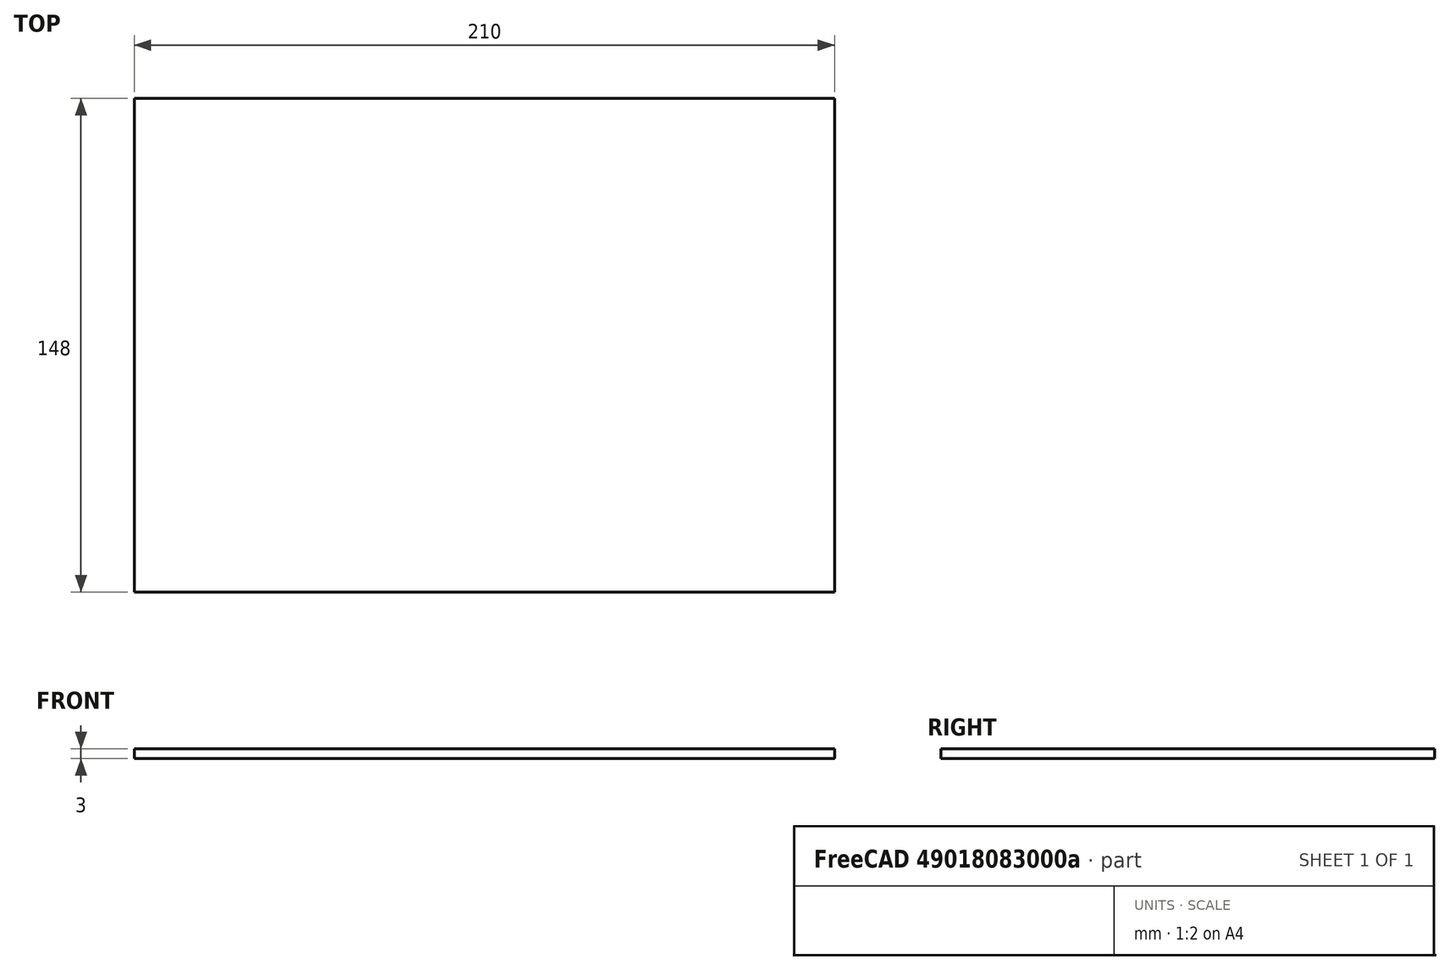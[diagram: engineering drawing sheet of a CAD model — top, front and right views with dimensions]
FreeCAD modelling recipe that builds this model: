
FCSTD DOCUMENT  (FreeCAD 0.20R29177 (Git))
Label: 1001_keyboard_button_labels_A5
License: All rights reserved
LicenseURL: http://en.wikipedia.org/wiki/All_rights_reserved
objects: Sketcher::SketchObject×5, PartDesign::Pad×1, PartDesign::Body×1
note: 8 computed .brp shape members not serialized (recipe doc carries the construction recipe); baked Part::Feature solids carry a one-line shape summary decoded from their .brp

FEATURE [Sketcher::SketchObject] Sketch
  FullyConstrained = true
  MapMode = 5
  Support = -> [XY_Plane]
  sketch-geometry (5):
    g0: LineSegment StartX=0 StartY=148 StartZ=0 EndX=210 EndY=148 EndZ=0
    g1: LineSegment StartX=210 StartY=148 StartZ=0 EndX=210 EndY=0 EndZ=0
    g2: LineSegment StartX=210 StartY=0 StartZ=0 EndX=0 EndY=0 EndZ=0
    g3: LineSegment StartX=0 StartY=0 StartZ=0 EndX=0 EndY=74 EndZ=0
    g4: LineSegment StartX=0 StartY=74 StartZ=0 EndX=0 EndY=148 EndZ=0
  constraints (14):
    c: Coincident(g0,g1)
    c: Coincident(g1,g2)
    c: Horizontal(g0)
    c: Horizontal(g2)
    c: Vertical(g1)
    c: DistanceY(g1,g1) = 148
    c: DistanceX(g0,g0) = 210
    c: Coincident(g3,g2)
    c: Coincident(g4,g0)
    c: Equal(g3,g4)
    c: Vertical(g4)
    c: Vertical(g3)
    c: Coincident(g3,g4)
    c: Coincident(g2,g-1)
FEATURE [PartDesign::Pad] Pad  label="A4_Landscape"
  AllowMultiFace = false
  Direction = (0,0,1)
  Length = 3
  Length2 = 100
  Profile = -> Sketch
  ReferenceAxis = -> Sketch [N_Axis]
  Type = 0
FEATURE [Sketcher::SketchObject] Sketch002  label="ButtonsLayoutSquare"
  FullyConstrained = false
  sketch-geometry (15):
    g0: LineSegment StartX=28.3334 StartY=64.9582 StartZ=0 EndX=28.3334 EndY=24.9582 EndZ=0
    g1: Circle CenterX=28.3334 CenterY=64.9582 CenterZ=0 NormalX=0 NormalY=0 NormalZ=1 AngleXU=0 Radius=15
    g2: Circle CenterX=28.3334 CenterY=24.9582 CenterZ=0 NormalX=0 NormalY=0 NormalZ=1 AngleXU=0 Radius=15
    g3: LineSegment StartX=28.3334 StartY=64.9582 StartZ=0 EndX=68.3334 EndY=64.9582 EndZ=0
    g4: LineSegment StartX=28.3334 StartY=24.9582 StartZ=0 EndX=68.3334 EndY=24.9582 EndZ=0
    g5: LineSegment StartX=68.3334 StartY=24.9582 StartZ=0 EndX=68.3334 EndY=64.9582 EndZ=0
    g6: Circle CenterX=68.3334 CenterY=64.9582 CenterZ=0 NormalX=0 NormalY=0 NormalZ=1 AngleXU=0 Radius=14.5
    g7: Circle CenterX=68.3334 CenterY=24.9582 CenterZ=0 NormalX=0 NormalY=0 NormalZ=1 AngleXU=0 Radius=15
    g8: LineSegment StartX=28.3334 StartY=24.9582 StartZ=0 EndX=48.3334 EndY=44.9582 EndZ=0
    g9: LineSegment StartX=48.3334 StartY=44.9582 StartZ=0 EndX=68.3334 EndY=64.9582 EndZ=0
    g10: LineSegment StartX=8.33338 StartY=84.9582 StartZ=0 EndX=8.33338 EndY=4.95818 EndZ=0
    g11: LineSegment StartX=8.33338 StartY=4.95818 StartZ=0 EndX=88.3334 EndY=4.95818 EndZ=0
    g12: LineSegment StartX=88.3334 StartY=4.95818 StartZ=0 EndX=88.3334 EndY=84.9582 EndZ=0
    g13: LineSegment StartX=88.3334 StartY=84.9582 StartZ=0 EndX=8.33338 EndY=84.9582 EndZ=0
    g14: Circle CenterX=48.3334 CenterY=44.9582 CenterZ=0 NormalX=0 NormalY=0 NormalZ=1 AngleXU=0 Radius=56.5685
  constraints (35):
    c: Equal(g2,g1)
    c: Coincident(g3,g1)
    c: Coincident(g4,g2)
    c: Coincident(g5,g4)
    c: Coincident(g5,g3)
    c: Equal(g3,g5)
    c: Equal(g5,g4)
    c: Coincident(g6,g3)
    c: Coincident(g7,g4)
    c: Coincident(g1,g0)
    c: Coincident(g0,g2)
    c: Angle(g0,g3) = 1.5708
    c: Distance(g6,g1) = 40
    c: Diameter(g6) = 29
    c: Vertical(g5)
    c: Vertical(g0)
    c: Coincident(g8,g2)
    c: Coincident(g9,g8)
    c: Coincident(g9,g6)
    c: Equal(g9,g8)
    c: Parallel(g9,g8)
    c: Coincident(g10,g11)
    c: Coincident(g11,g12)
    c: Coincident(g12,g13)
    c: Coincident(g13,g10)
    c: Equal(g10,g11)
    c: Equal(g10,g12)
    c: Equal(g10,g13)
    c: PointOnObject(g10,g14)
    c: PointOnObject(g11,g14)
    c: PointOnObject(g12,g14)
    c: PointOnObject(g13,g14)
    c: Coincident(g14,g8)
    c: Horizontal(g13)
    c: DistanceX(g13,g13) = 80
FEATURE [Sketcher::SketchObject] Sketch008  label="ButtonsLayoutLTLS"
  FullyConstrained = false
  sketch-geometry (20):
    g0: Circle CenterX=128.028 CenterY=71.1546 CenterZ=0 NormalX=0 NormalY=0 NormalZ=1 AngleXU=0 Radius=15
    g1: Circle CenterX=168.028 CenterY=71.1546 CenterZ=0 NormalX=0 NormalY=0 NormalZ=1 AngleXU=0 Radius=14.5
    g2: LineSegment StartX=188.028 StartY=91.1546 StartZ=0 EndX=108.028 EndY=91.1546 EndZ=0
    g3: LineSegment StartX=148.028 StartY=51.1546 StartZ=0 EndX=108.028 EndY=51.1546 EndZ=0
    g4: LineSegment StartX=148.028 StartY=51.1546 StartZ=0 EndX=188.028 EndY=51.1546 EndZ=0
    g5: LineSegment StartX=188.028 StartY=91.1546 StartZ=0 EndX=188.028 EndY=51.1546 EndZ=0
    g6: LineSegment StartX=108.028 StartY=91.1546 StartZ=0 EndX=108.028 EndY=71.1546 EndZ=0
    g7: LineSegment StartX=108.028 StartY=71.1546 StartZ=0 EndX=108.028 EndY=51.1546 EndZ=0
    g8: LineSegment StartX=128.028 StartY=71.1546 StartZ=0 EndX=148.028 EndY=71.1546 EndZ=0
    g9: LineSegment StartX=148.028 StartY=71.1546 StartZ=0 EndX=168.028 EndY=71.1546 EndZ=0
    g10: Circle CenterX=128.715 CenterY=25.6447 CenterZ=0 NormalX=0 NormalY=0 NormalZ=1 AngleXU=0 Radius=15
    g11: Circle CenterX=168.715 CenterY=25.6447 CenterZ=0 NormalX=0 NormalY=0 NormalZ=1 AngleXU=0 Radius=14.5
    g12: LineSegment StartX=188.715 StartY=45.6447 StartZ=0 EndX=108.715 EndY=45.6447 EndZ=0
    g13: LineSegment StartX=148.715 StartY=5.64469 StartZ=0 EndX=108.715 EndY=5.64469 EndZ=0
    g14: LineSegment StartX=148.715 StartY=5.64469 StartZ=0 EndX=188.715 EndY=5.64469 EndZ=0
    g15: LineSegment StartX=188.715 StartY=45.6447 StartZ=0 EndX=188.715 EndY=5.64469 EndZ=0
    g16: LineSegment StartX=108.715 StartY=45.6447 StartZ=0 EndX=108.715 EndY=25.6447 EndZ=0
    g17: LineSegment StartX=108.715 StartY=25.6447 StartZ=0 EndX=108.715 EndY=5.64469 EndZ=0
    g18: LineSegment StartX=128.715 StartY=25.6447 StartZ=0 EndX=148.715 EndY=25.6447 EndZ=0
    g19: LineSegment StartX=148.715 StartY=25.6447 StartZ=0 EndX=168.715 EndY=25.6447 EndZ=0
  constraints (52):
    c: Distance(g1,g0) = 40
    c: Diameter(g1) = 29
    c: Horizontal(g2)
    c: DistanceX(g2,g2) = 80
    c: Horizontal(g3)
    c: Coincident(g4,g3)
    c: Horizontal(g4)
    c: Coincident(g5,g2)
    c: Coincident(g5,g4)
    c: Vertical(g5)
    c: Coincident(g6,g2)
    c: Vertical(g6)
    c: Coincident(g7,g6)
    c: Coincident(g7,g3)
    c: Vertical(g7)
    c: Coincident(g8,g0)
    c: Horizontal(g8)
    c: Coincident(g9,g8)
    c: Coincident(g9,g1)
    c: Horizontal(g9)
    c: Horizontal(g0,g6)
    c: Vertical(g8,g3)
    c: Equal(g7,g6)
    c: Equal(g4,g3)
    c: Equal(g9,g8)
    c: DistanceY(g5,g5) = 40
    c: Distance(g11,g10) = 40
    c: Diameter(g11) = 29
    c: Horizontal(g12)
    c: DistanceX(g12,g12) = 80
    c: Horizontal(g13)
    c: Coincident(g14,g13)
    c: Horizontal(g14)
    c: Coincident(g15,g12)
    c: Coincident(g15,g14)
    c: Vertical(g15)
    c: Coincident(g16,g12)
    c: Vertical(g16)
    c: Coincident(g17,g16)
    c: Coincident(g17,g13)
    c: Vertical(g17)
    c: Coincident(g18,g10)
    c: Horizontal(g18)
    c: Coincident(g19,g18)
    c: Coincident(g19,g11)
    c: Horizontal(g19)
    c: Horizontal(g10,g16)
    c: Vertical(g18,g13)
    c: Equal(g17,g16)
    c: Equal(g14,g13)
    c: Equal(g19,g18)
    c: DistanceY(g15,g15) = 40
FEATURE [Sketcher::SketchObject] Sketch009  label="ButtonsLayoutSelHotStart"
  FullyConstrained = false
  sketch-geometry (12):
    g0: Circle CenterX=68.3334 CenterY=117.764 CenterZ=0 NormalX=0 NormalY=0 NormalZ=1 AngleXU=0 Radius=15
    g1: Circle CenterX=28.3334 CenterY=117.764 CenterZ=0 NormalX=0 NormalY=0 NormalZ=1 AngleXU=0 Radius=15
    g2: LineSegment StartX=68.3334 StartY=117.764 StartZ=0 EndX=108.333 EndY=117.764 EndZ=0
    g3: Circle CenterX=108.333 CenterY=117.764 CenterZ=0 NormalX=0 NormalY=0 NormalZ=1 AngleXU=0 Radius=14.5
    g4: LineSegment StartX=68.3334 StartY=117.764 StartZ=0 EndX=28.3334 EndY=117.764 EndZ=0
    g5: LineSegment StartX=68.3334 StartY=117.764 StartZ=0 EndX=68.3334 EndY=137.764 EndZ=0
    g6: LineSegment StartX=68.3334 StartY=137.764 StartZ=0 EndX=8.33338 EndY=137.764 EndZ=0
    g7: LineSegment StartX=8.33338 StartY=137.764 StartZ=0 EndX=8.33338 EndY=97.764 EndZ=0
    g8: LineSegment StartX=8.33338 StartY=97.764 StartZ=0 EndX=128.333 EndY=97.764 EndZ=0
    g9: LineSegment StartX=128.333 StartY=97.764 StartZ=0 EndX=128.333 EndY=117.764 EndZ=0
    g10: LineSegment StartX=128.333 StartY=117.764 StartZ=0 EndX=128.333 EndY=137.764 EndZ=0
    g11: LineSegment StartX=128.333 StartY=137.764 StartZ=0 EndX=68.3334 EndY=137.764 EndZ=0
  constraints (30):
    c: Equal(g1,g0)
    c: Coincident(g2,g0)
    c: Coincident(g3,g2)
    c: Distance(g3,g0) = 40
    c: Diameter(g3) = 29
    c: Coincident(g4,g0)
    c: Coincident(g4,g1)
    c: Equal(g4,g2)
    c: Horizontal(g4)
    c: Coincident(g5,g0)
    c: Vertical(g5)
    c: Coincident(g6,g5)
    c: Horizontal(g6)
    c: Coincident(g7,g6)
    c: Vertical(g7)
    c: Horizontal(g8)
    c: Coincident(g9,g8)
    c: Vertical(g9)
    c: Coincident(g10,g9)
    c: Vertical(g10)
    c: Coincident(g11,g10)
    c: Coincident(g11,g6)
    c: Horizontal(g11)
    c: Horizontal(g9,g3)
    c: Equal(g11,g6)
    c: Coincident(g8,g7)
    c: Equal(g9,g10)
    c: Horizontal(g2)
    c: DistanceY(g7,g7) = 40
    c: DistanceX(g6,g10) = 120
FEATURE [Sketcher::SketchObject] Sketch010
  FullyConstrained = false
  MapMode = 5
  Support = -> [XY_Plane]
  sketch-geometry (45):
    g0: Circle CenterX=68.0905 CenterY=65.8823 CenterZ=0 NormalX=0 NormalY=0 NormalZ=1 AngleXU=0 Radius=9
    g1: LineSegment StartX=65.5172 StartY=59.9412 StartZ=0 EndX=62.9322 EndY=59.9412 EndZ=0
    g2: LineSegment StartX=62.9322 StartY=59.9412 StartZ=0 EndX=66.087 EndY=71.9412 EndZ=0
    g3: LineSegment StartX=66.087 StartY=71.9412 StartZ=0 EndX=67.512 EndY=67.529 EndZ=0
    g4: LineSegment StartX=67.512 StartY=67.529 StartZ=0 EndX=65.5172 EndY=59.9412 EndZ=0
    g5: LineSegment StartX=67.1378 StartY=71.9412 StartZ=0 EndX=69.765 EndY=71.9412 EndZ=0
    g6: LineSegment StartX=69.765 StartY=71.9412 StartZ=0 EndX=73.6407 EndY=59.9412 EndZ=0
    g7: LineSegment StartX=73.6407 StartY=59.9412 StartZ=0 EndX=71.0558 EndY=59.9412 EndZ=0
    g8: LineSegment StartX=71.0558 StartY=59.9412 StartZ=0 EndX=70.2347 EndY=62.4835 EndZ=0
    g9: LineSegment StartX=68.0835 StartY=64.9835 StartZ=0 EndX=69.385 EndY=64.9835 EndZ=0
    g10: LineSegment StartX=69.385 StartY=64.9835 StartZ=0 EndX=67.1378 EndY=71.9412 EndZ=0
    g11: LineSegment StartX=67.512 StartY=67.529 StartZ=0 EndX=65.0941 EndY=68.1646 EndZ=0
    g12: LineSegment StartX=70.2347 StartY=62.4835 StartZ=0 EndX=67.4263 EndY=62.4835 EndZ=0
    g13: LineSegment StartX=67.4263 StartY=62.4835 StartZ=0 EndX=68.0835 EndY=64.9835 EndZ=0
    g14: LineSegment StartX=69.385 StartY=64.9835 StartZ=0 EndX=71.764 EndY=65.7518 EndZ=0
    g15: LineSegment StartX=69.385 StartY=64.9835 StartZ=0 EndX=69.385 EndY=62.4835 EndZ=0
    g16: Circle CenterX=28.3099 CenterY=64.6257 CenterZ=0 NormalX=0 NormalY=0 NormalZ=1 AngleXU=0 Radius=9
    g17: LineSegment StartX=24.5219 StartY=70.219 StartZ=0 EndX=24.5219 EndY=59.0563 EndZ=0
    g18: LineSegment StartX=24.5219 StartY=59.0563 StartZ=0 EndX=27.0219 EndY=59.0563 EndZ=0
    g19: LineSegment StartX=27.0219 StartY=59.0563 StartZ=0 EndX=27.0219 EndY=70.219 EndZ=0
    g20: LineSegment StartX=27.0219 StartY=70.219 StartZ=0 EndX=24.5219 EndY=70.219 EndZ=0
    g21: LineSegment StartX=30.5219 StartY=70.219 StartZ=0 EndX=30.5219 EndY=67.719 EndZ=0
    g22: LineSegment StartX=30.5219 StartY=65.8876 StartZ=0 EndX=30.5219 EndY=63.3876 EndZ=0
    g23: LineSegment StartX=30.5219 StartY=61.5563 StartZ=0 EndX=30.5219 EndY=59.0563 EndZ=0
    g24: LineSegment StartX=30.5219 StartY=67.719 StartZ=0 EndX=30.5219 EndY=66.8033 EndZ=0
    g25: LineSegment StartX=30.5219 StartY=66.8033 StartZ=0 EndX=30.5219 EndY=65.8876 EndZ=0
    g26: LineSegment StartX=30.5219 StartY=63.3876 StartZ=0 EndX=30.5219 EndY=62.472 EndZ=0
    g27: LineSegment StartX=30.5219 StartY=62.472 StartZ=0 EndX=30.5219 EndY=61.5563 EndZ=0
    g28: ArcOfCircle CenterX=30.5219 CenterY=62.472 CenterZ=0 NormalX=0 NormalY=0 NormalZ=1 AngleXU=0 Radius=0.915669 StartAngle=4.71239 EndAngle=7.85398
    g29: ArcOfCircle CenterX=30.5219 CenterY=66.8033 CenterZ=0 NormalX=0 NormalY=0 NormalZ=1 AngleXU=0 Radius=0.915669 StartAngle=4.71239 EndAngle=7.85398
    g30: ArcOfCircle CenterX=30.5219 CenterY=66.8033 CenterZ=0 NormalX=0 NormalY=0 NormalZ=1 AngleXU=0 Radius=3.41567 StartAngle=5.59642 EndAngle=7.85398
    g31: ArcOfCircle CenterX=30.5219 CenterY=62.472 CenterZ=0 NormalX=0 NormalY=0 NormalZ=1 AngleXU=0 Radius=3.41567 StartAngle=4.71239 EndAngle=6.96995
    g32: LineSegment StartX=30.5219 StartY=59.0563 StartZ=0 EndX=28.0219 EndY=59.0563 EndZ=0
    g33: LineSegment StartX=28.0219 StartY=59.0563 StartZ=0 EndX=28.0219 EndY=61.5563 EndZ=0
    g34: LineSegment StartX=28.0219 StartY=61.5563 StartZ=0 EndX=30.5219 EndY=61.5563 EndZ=0
    g35: LineSegment StartX=30.5219 StartY=61.5563 StartZ=0 EndX=30.5219 EndY=59.0563 EndZ=0
    g36: LineSegment StartX=30.5219 StartY=63.3876 StartZ=0 EndX=28.0219 EndY=63.3876 EndZ=0
    g37: LineSegment StartX=28.0219 StartY=63.3876 StartZ=0 EndX=28.0219 EndY=65.8876 EndZ=0
    g38: LineSegment StartX=28.0219 StartY=65.8876 StartZ=0 EndX=30.5219 EndY=65.8876 EndZ=0
    g39: LineSegment StartX=30.5219 StartY=65.8876 StartZ=0 EndX=30.5219 EndY=63.3876 EndZ=0
    g40: LineSegment StartX=30.5219 StartY=67.719 StartZ=0 EndX=28.0219 EndY=67.719 EndZ=0
    g41: LineSegment StartX=28.0219 StartY=67.719 StartZ=0 EndX=28.0219 EndY=70.219 EndZ=0
    g42: LineSegment StartX=28.0219 StartY=70.219 StartZ=0 EndX=30.5219 EndY=70.219 EndZ=0
    g43: LineSegment StartX=30.5219 StartY=70.219 StartZ=0 EndX=30.5219 EndY=67.719 EndZ=0
    g44: LineSegment StartX=67.512 StartY=67.529 StartZ=0 EndX=68.4636 EndY=67.8364 EndZ=0
  constraints (114):
    c: Diameter(g0) = 18
    c: Horizontal(g1)
    c: Coincident(g1,g2)
    c: Coincident(g2,g3)
    c: Coincident(g3,g4)
    c: Coincident(g4,g1)
    c: Coincident(g5,g6)
    c: Coincident(g6,g7)
    c: Horizontal(g7)
    c: Coincident(g7,g8)
    c: Coincident(g9,g10)
    c: Coincident(g10,g5)
    c: Equal(g1,g7)
    c: Coincident(g11,g3)
    c: PointOnObject(g11,g2)
    c: Perpendicular(g2,g11)
    c: Parallel(g4,g2)
    c: Parallel(g10,g6)
    c: Parallel(g8,g6)
    c: Coincident(g12,g8)
    c: Horizontal(g12)
    c: Coincident(g13,g12)
    c: Coincident(g13,g9)
    c: Parallel(g13,g4)
    c: Horizontal(g7,g1)
    c: Coincident(g14,g9)
    c: PointOnObject(g14,g6)
    c: Perpendicular(g6,g14)
    c: Equal(g14,g11)
    c: Horizontal(g9)
    c: Distance(g14) = 2.5
    c: Parallel(g3,g10)
    c: Horizontal(g5,g2)
    c: Horizontal(g5)
    c: Coincident(g15,g9)
    c: PointOnObject(g15,g12)
    c: Vertical(g15)
    c: Equal(g15,g14)
    c: DistanceY(g1,g2) = 12
    c: Equal(g16,g0)
    c: Vertical(g17)
    c: Coincident(g17,g18)
    c: Horizontal(g18)
    c: Coincident(g18,g19)
    c: Vertical(g19)
    c: Coincident(g19,g20)
    c: Coincident(g20,g17)
    c: Horizontal(g20)
    c: Vertical(g21)
    c: Vertical(g22)
    c: Vertical(g23)
    c: Horizontal(g23,g18)
    c: Horizontal(g21,g19)
    c: Equal(g21,g22)
    c: Equal(g22,g23)
    c: Coincident(g21,g24)
    c: Vertical(g24)
    c: Coincident(g24,g25)
    c: Coincident(g25,g22)
    c: Vertical(g25)
    c: Coincident(g22,g26)
    c: Coincident(g26,g27)
    c: Coincident(g27,g23)
    c: Equal(g26,g25)
    c: Coincident(g28,g26)
    c: Coincident(g28,g22)
    c: Coincident(g28,g23)
    c: Coincident(g29,g24)
    c: Coincident(g29,g22)
    c: Coincident(g29,g21)
    c: Coincident(g30,g24)
    c: Coincident(g30,g21)
    c: Coincident(g31,g26)
    c: Coincident(g31,g23)
    c: Coincident(g30,g31)
    c: Coincident(g32,g33)
    c: Coincident(g33,g34)
    c: Coincident(g34,g35)
    c: Coincident(g35,g32)
    c: Horizontal(g32)
    c: Horizontal(g34)
    c: Vertical(g33)
    c: Coincident(g32,g23)
    c: Coincident(g36,g37)
    c: Coincident(g37,g38)
    c: Coincident(g38,g39)
    c: Coincident(g39,g36)
    c: Horizontal(g36)
    c: Horizontal(g38)
    c: Vertical(g37)
    c: Coincident(g36,g22)
    c: Coincident(g40,g41)
    c: Coincident(g41,g42)
    c: Coincident(g42,g43)
    c: Coincident(g43,g40)
    c: Horizontal(g40)
    c: Horizontal(g42)
    c: Vertical(g41)
    c: Coincident(g40,g21)
    c: Coincident(g42,g21)
    c: Coincident(g38,g22)
    c: Coincident(g34,g23)
    c: Vertical(g27)
    c: Vertical(g26)
    c: Vertical(g33,g36)
    c: Vertical(g37,g40)
    c: Equal(g33,g18)
    c: Equal(g20,g42)
    c: DistanceX(g19,g41) = 1
    c: DistanceX(g18,g18) = 2.5
    c: Coincident(g44,g3)
    c: PointOnObject(g44,g10)
    c: Perpendicular(g3,g44)
    c: Distance(g44) = 1
FEATURE [PartDesign::Body] Body
  Group = -> [Sketch,Pad,Sketch010]
  Origin = -> Origin
  Tip = -> Pad
